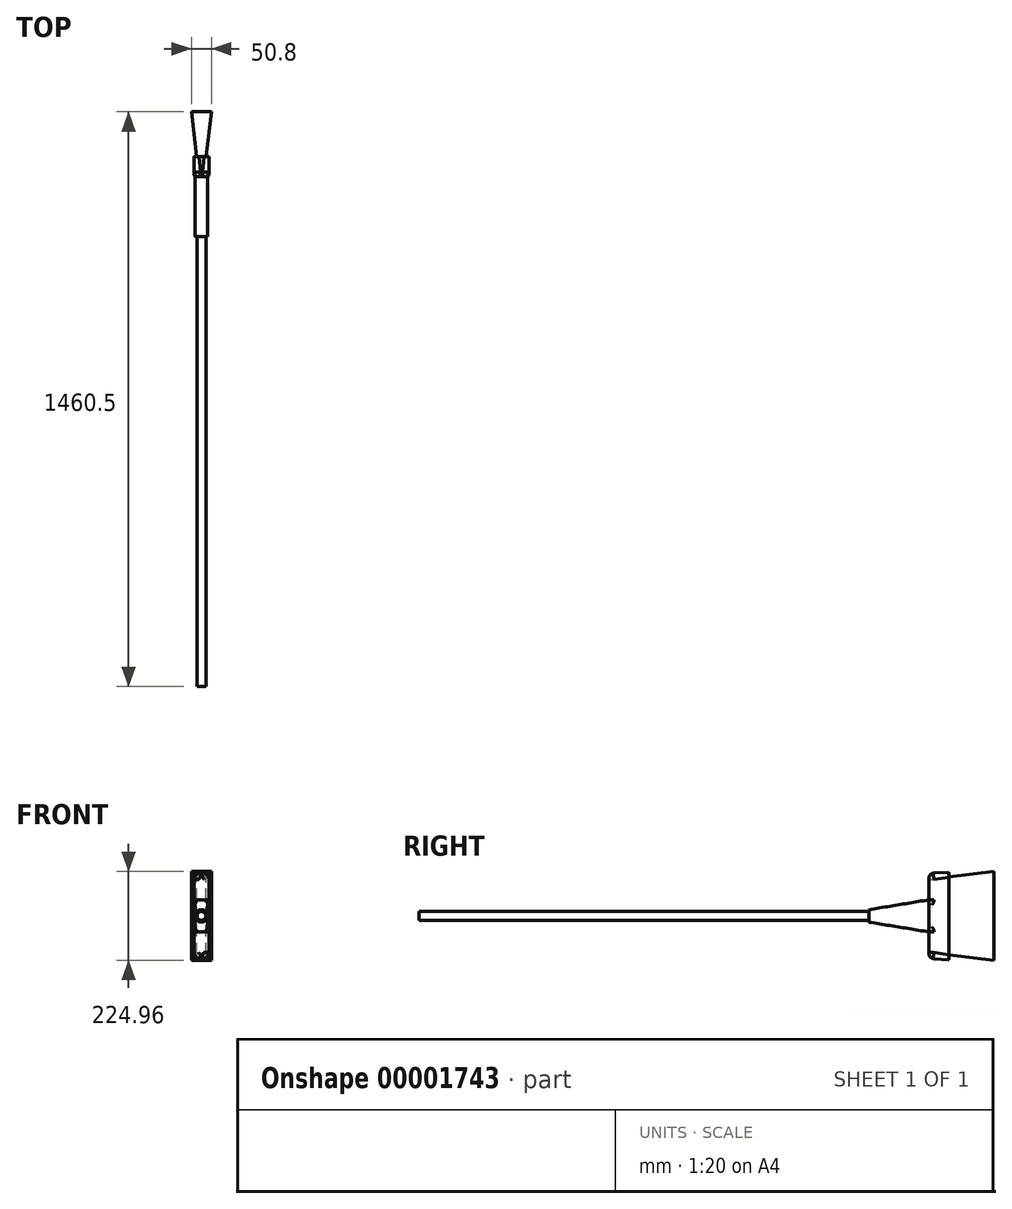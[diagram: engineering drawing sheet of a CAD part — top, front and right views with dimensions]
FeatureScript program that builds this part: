
annotation { "Feature Type Name" : "Feature", "Feature Type Description" : "" }
export const myFeature = defineFeature(function(context is Context, id is Id, definition is map)
    precondition{}
    {
        {
            var Q0;
            Q0=qCreatedBy(makeId("Front.planeOp"),FACE);
            var sketch = newSketch(context, id + "F0", { "sketchPlane" : qUnion([Q0])});
            skCircle(sketch, "E0", {"center": v(0, 0) * mm, "radius": 11.11 * mm});
            skSolve(sketch);
        }
        {
            var Q0;
            Q0=makeQuery(id+"F0.imprint","IMPRINT",FACE,{"disambiguationData":[TD([[makeQuery(id+"F0.imprint","IMPRINT",EDGE,{"derivedFrom":sQuery(id+"F0.wireOp",EDGE,"E0")}),1.0]])]});
            extrude(context, id + "F1", {"entities" : qUnion([Q0]), "depth" : 1143 * mm});
        }
        {
            var Q0;
            Q0=qCreatedBy(makeId("Front.planeOp"),FACE);
            var sketch = newSketch(context, id + "F2", { "sketchPlane" : qUnion([Q0])});
            skCircle(sketch, "E1", {"center": v(0, 0) * mm, "radius": 15.88 * mm});
            skSolve(sketch);
        }
        {
            var Q0;
            Q0=qCreatedBy(makeId("Front.planeOp"),FACE);
            cPlane(context, id + "F3", {"entities" : qUnion([Q0]), "cplaneType" : CPlaneType.OFFSET, "offset" : 152.4 * mm, "oppositeDirection" : true, "width" : 152.4 * mm, "height" : 152.4 * mm});
        }
        {
            var Q0;
            Q0=qCreatedBy(id+"F3.planeOp",FACE);
            var sketch = newSketch(context, id + "F4", { "sketchPlane" : qUnion([Q0])});
            skLineSegment(sketch, "E2.rect.bottom", {"start": v(3.17, 40.83) * mm, "end": v(-3.17, 40.83) * mm});
            skLineSegment(sketch, "E2.rect.top", {"start": v(3.17, -40.83) * mm, "end": v(-3.17, -40.83) * mm});
            skLineSegment(sketch, "E2.rect.left", {"start": v(15.88, 28.13) * mm, "end": v(15.88, -28.13) * mm});
            skLineSegment(sketch, "E2.rect.right", {"start": v(-15.88, 28.13) * mm, "end": v(-15.88, -28.13) * mm});
            skPoint(sketch, "E2.rect.middle", {"position": v(0, 0) * mm});
            skPoint(sketch, "E3.visualSharp", {"position": v(-15.88, -40.83) * mm});
            skArc(sketch, "E3.filletArc", {"start": v(-15.87, -28.13) * mm, "mid": v(-12.16, -37.1) * mm, "end": v(-3.17, -40.83) * mm});
            skPoint(sketch, "E4.visualSharp", {"position": v(15.88, -40.83) * mm});
            skArc(sketch, "E4.filletArc", {"start": v(3.17, -40.83) * mm, "mid": v(12.16, -37.1) * mm, "end": v(15.88, -28.13) * mm});
            skPoint(sketch, "E5.visualSharp", {"position": v(15.88, 40.83) * mm});
            skArc(sketch, "E5.filletArc", {"start": v(15.88, 28.13) * mm, "mid": v(12.16, 37.1) * mm, "end": v(3.17, 40.83) * mm});
            skPoint(sketch, "E6.visualSharp", {"position": v(-15.88, 40.83) * mm});
            skArc(sketch, "E6.filletArc", {"start": v(-3.17, 40.83) * mm, "mid": v(-12.16, 37.1) * mm, "end": v(-15.88, 28.13) * mm});
            skSolve(sketch);
        }
        {
            var Q1;
            Q1=makeQuery(id+"F4.imprint","IMPRINT",FACE,{"disambiguationData":[TD([[makeQuery(id+"F4.imprint","IMPRINT",EDGE,{"derivedFrom":sQuery(id+"F4.wireOp",EDGE,"E2.rect.bottom")}),1.0]])]});
            var Q2;
            Q2=makeQuery(id+"F2.imprint","IMPRINT",FACE,{"disambiguationData":[TD([[makeQuery(id+"F2.imprint","IMPRINT",EDGE,{"derivedFrom":sQuery(id+"F2.wireOp",EDGE,"E1")}),1.0]])]});
            loft(context, id + "F5", {"operationType" : NewBodyOperationType.ADD, "sheetProfilesArray" : [{ "sheetProfileEntities" : qUnion([Q1]) }, { "sheetProfileEntities" : qUnion([Q2]) }]});
        }
        {
            var Q0;
            Q0=qCreatedBy(id+"F3.planeOp",FACE);
            var sketch = newSketch(context, id + "F6", { "sketchPlane" : qUnion([Q0])});
            skLineSegment(sketch, "E7.rect.bottom", {"start": v(1.27, -107.95) * mm, "end": v(-1.27, -107.95) * mm});
            skLineSegment(sketch, "E7.rect.top", {"start": v(1.27, 107.95) * mm, "end": v(-1.27, 107.95) * mm});
            skLineSegment(sketch, "E7.rect.left", {"start": v(19.05, -90.17) * mm, "end": v(19.05, 90.17) * mm});
            skLineSegment(sketch, "E7.rect.right", {"start": v(-19.05, -90.17) * mm, "end": v(-19.05, 90.17) * mm});
            skPoint(sketch, "E7.rect.middle", {"position": v(0, 0) * mm});
            skPoint(sketch, "E8.visualSharp", {"position": v(19.05, -107.95) * mm});
            skArc(sketch, "E8.filletArc", {"start": v(1.27, -107.95) * mm, "mid": v(13.84, -102.74) * mm, "end": v(19.05, -90.17) * mm});
            skPoint(sketch, "E9.visualSharp", {"position": v(-19.05, -107.95) * mm});
            skArc(sketch, "E9.filletArc", {"start": v(-19.05, -90.17) * mm, "mid": v(-13.84, -102.74) * mm, "end": v(-1.27, -107.95) * mm});
            skPoint(sketch, "E10.visualSharp", {"position": v(-19.05, 107.95) * mm});
            skArc(sketch, "E10.filletArc", {"start": v(-1.27, 107.95) * mm, "mid": v(-13.84, 102.74) * mm, "end": v(-19.05, 90.17) * mm});
            skPoint(sketch, "E11.visualSharp", {"position": v(19.05, 107.95) * mm});
            skArc(sketch, "E11.filletArc", {"start": v(19.05, 90.17) * mm, "mid": v(13.84, 102.74) * mm, "end": v(1.27, 107.95) * mm});
            skSolve(sketch);
        }
        {
            var Q0;
            Q0=qCreatedBy(id+"F3.planeOp",FACE);
            cPlane(context, id + "F7", {"entities" : qUnion([Q0]), "cplaneType" : CPlaneType.OFFSET, "offset" : 50.8 * mm, "oppositeDirection" : true, "width" : 152.4 * mm, "height" : 152.4 * mm});
        }
        {
            var Q0;
            Q0=qCreatedBy(id+"F7.planeOp",FACE);
            var sketch = newSketch(context, id + "F8", { "sketchPlane" : qUnion([Q0])});
            skLineSegment(sketch, "E12.rect.bottom", {"start": v(6.35, -111.13) * mm, "end": v(-6.35, -111.13) * mm});
            skLineSegment(sketch, "E12.rect.top", {"start": v(6.35, 111.12) * mm, "end": v(-6.35, 111.12) * mm});
            skLineSegment(sketch, "E12.rect.left", {"start": v(19.05, -98.43) * mm, "end": v(19.05, 98.42) * mm});
            skLineSegment(sketch, "E12.rect.right", {"start": v(-19.05, -98.43) * mm, "end": v(-19.05, 98.42) * mm});
            skPoint(sketch, "E12.rect.middle", {"position": v(0, 0) * mm});
            skPoint(sketch, "E13.visualSharp", {"position": v(19.05, -111.13) * mm});
            skArc(sketch, "E13.filletArc", {"start": v(6.35, -111.13) * mm, "mid": v(15.33, -107.4) * mm, "end": v(19.05, -98.43) * mm});
            skPoint(sketch, "E14.visualSharp", {"position": v(-19.05, -111.13) * mm});
            skArc(sketch, "E14.filletArc", {"start": v(-19.05, -98.43) * mm, "mid": v(-15.33, -107.4) * mm, "end": v(-6.35, -111.13) * mm});
            skPoint(sketch, "E15.visualSharp", {"position": v(-19.05, 111.12) * mm});
            skArc(sketch, "E15.filletArc", {"start": v(-6.35, 111.12) * mm, "mid": v(-15.33, 107.4) * mm, "end": v(-19.05, 98.42) * mm});
            skPoint(sketch, "E16.visualSharp", {"position": v(19.05, 111.12) * mm});
            skArc(sketch, "E16.filletArc", {"start": v(19.05, 98.42) * mm, "mid": v(15.33, 107.4) * mm, "end": v(6.35, 111.12) * mm});
            skSolve(sketch);
        }
        {
            var Q1;
            Q1=makeQuery(id+"F6.imprint","IMPRINT",FACE,{"disambiguationData":[TD([[makeQuery(id+"F6.imprint","IMPRINT",EDGE,{"derivedFrom":sQuery(id+"F6.wireOp",EDGE,"E7.rect.bottom")}),-1.0]])]});
            var Q2;
            Q2=makeQuery(id+"F8.imprint","IMPRINT",FACE,{"disambiguationData":[TD([[makeQuery(id+"F8.imprint","IMPRINT",EDGE,{"derivedFrom":sQuery(id+"F8.wireOp",EDGE,"E12.rect.bottom")}),-1.0]])]});
            loft(context, id + "F9", {"operationType" : NewBodyOperationType.ADD, "sheetProfilesArray" : [{ "sheetProfileEntities" : qUnion([Q1]) }, { "sheetProfileEntities" : qUnion([Q2]) }]});
        }
        {
            var Q0;
            Q0=makeQuery(id+"F9.opLoft","MID_CAP_EDGE",EDGE,{"disambiguationData":[OSD([sQuery(id+"F6.wireOp",EDGE,"E7.rect.bottom"),sQuery(id+"F6.wireOp",EDGE,"E7.rect.right"),sQuery(id+"F6.wireOp",EDGE,"E9.filletArc")])],"capPos":0.0});
            fillet(context, id + "F10", {"entities" : qUnion([Q0]), "radius" : 12.7 * mm, "tangentPropagation" : true, "allowEdgeOverflow" : false});
        }
        {
            var Q0;
            Q0=qCreatedBy(id+"F7.planeOp",FACE);
            var sketch = newSketch(context, id + "F11", { "sketchPlane" : qUnion([Q0])});
            skLineSegment(sketch, "E17.rect.bottom", {"start": v(12.18, -98.58) * mm, "end": v(-12.18, -98.58) * mm});
            skLineSegment(sketch, "E17.rect.top", {"start": v(12.18, 98.58) * mm, "end": v(-12.18, 98.58) * mm});
            skLineSegment(sketch, "E17.rect.left", {"start": v(12.18, -98.58) * mm, "end": v(12.18, 98.58) * mm});
            skLineSegment(sketch, "E17.rect.right", {"start": v(-12.18, -98.58) * mm, "end": v(-12.18, 98.58) * mm});
            skPoint(sketch, "E17.rect.middle", {"position": v(0, 0) * mm});
            skSolve(sketch);
        }
        {
            var Q0;
            Q0=qCreatedBy(id+"F7.planeOp",FACE);
            cPlane(context, id + "F12", {"entities" : qUnion([Q0]), "cplaneType" : CPlaneType.OFFSET, "offset" : 114.3 * mm, "oppositeDirection" : true, "width" : 152.4 * mm, "height" : 152.4 * mm});
        }
        {
            var Q0;
            Q0=qCreatedBy(id+"F12.planeOp",FACE);
            var sketch = newSketch(context, id + "F13", { "sketchPlane" : qUnion([Q0])});
            skLineSegment(sketch, "E18.rect.bottom", {"start": v(25.4, -112.48) * mm, "end": v(-25.4, -112.48) * mm});
            skLineSegment(sketch, "E18.rect.top", {"start": v(25.4, 112.48) * mm, "end": v(-25.4, 112.48) * mm});
            skLineSegment(sketch, "E18.rect.left", {"start": v(25.4, -112.48) * mm, "end": v(25.4, 112.48) * mm});
            skLineSegment(sketch, "E18.rect.right", {"start": v(-25.4, -112.48) * mm, "end": v(-25.4, 112.48) * mm});
            skPoint(sketch, "E18.rect.middle", {"position": v(0, 0) * mm});
            skSolve(sketch);
        }
        {
            var Q1;
            Q1=makeQuery(id+"F13.imprint","IMPRINT",FACE,{"disambiguationData":[TD([[makeQuery(id+"F13.imprint","IMPRINT",EDGE,{"derivedFrom":sQuery(id+"F13.wireOp",EDGE,"E18.rect.bottom")}),-1.0]])]});
            var Q2;
            Q2=makeQuery(id+"F11.imprint","IMPRINT",FACE,{"disambiguationData":[TD([[makeQuery(id+"F11.imprint","IMPRINT",EDGE,{"derivedFrom":sQuery(id+"F11.wireOp",EDGE,"E17.rect.bottom")}),-1.0]])]});
            loft(context, id + "F14", {"operationType" : NewBodyOperationType.ADD, "sheetProfilesArray" : [{ "sheetProfileEntities" : qUnion([Q1]) }, { "sheetProfileEntities" : qUnion([Q2]) }]});
        }
        {
            var Q0;
            Q0=qCreatedBy(makeId("Right.planeOp"),FACE);
            var sketch = newSketch(context, id + "F15", { "sketchPlane" : qUnion([Q0])});
            skLineSegment(sketch, "E19", {"start": v(0, 0) * mm, "end": v(115.66, 0) * mm, "construction": true});
            skLineSegment(sketch, "E20", {"start": v(115.66, 0) * mm, "end": v(115.66, -62.17) * mm, "construction": true});
            skSolve(sketch);
        }
    });
